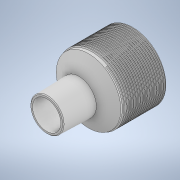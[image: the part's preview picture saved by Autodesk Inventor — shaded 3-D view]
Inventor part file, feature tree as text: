
AUTODESK INVENTOR PART (.ipt)
format: ipt  version: 2020 (Build 240168000, 168)  size: 853,504 bytes
history: native  units: mm
features: sketch x14, extrude x9, chamfer x6, revolve x3, helix x2, plane x2, split x1, projected_geometry x1
ambient origin geometry x8: Origin, YZ Plane, XZ Plane, XY Plane, X Axis, Y Axis, Z Axis, Center Point
bodies: Solid1 (feature_tree)
feature tree (38):
  extrude  "Extrusion1"  Depth=2.0mm
  chamfer  "Chamfer1"  Distance=2.0mm
  revolve  "Revolution1"  [1 undecoded]
  extrude  "Extrusion2"  Depth=18.75mm
  sketch  "Sketch6"  dims[d17=1.6mm]
  helix  "Coil2"  [1 undecoded]
  chamfer  "Chamfer4"  Distance=10.0mm
  chamfer  "Chamfer5"  Distance=0.65mm Angle=45.0deg
  extrude  "Extrusion4"  Depth=42.0mm
  extrude  "Extrusion6"  Depth=10.0mm
  extrude  "Extrusion7"  Depth=10.0mm
  helix  "Coil3"  [1 undecoded]
  extrude  "Extrusion8"  Depth=10.0mm TaperAngle=0.0deg
  revolve  "Revolution2"  [1 undecoded]
  extrude  "Extrusion9"  Depth=10.0mm TaperAngle=0.0deg
  plane  "Work Plane3"
  split  "Split2"
  revolve  "Revolution3"  [1 undecoded]
  plane  "Work Plane4"
  extrude  "Extrusion10"  Depth=10.0mm
  chamfer  "Chamfer9"  Distance=1.5mm
  chamfer  "Chamfer10"  Distance=45.0mm
  chamfer  "Chamfer13"  Distance=20.0mm
  extrude  "Extrusion11"  TaperAngle=135.0deg  [1 undecoded]
  sketch  "Sketch1"  dims[d0=18.0mm d1=2.0mm d2=2.0mm d3=0.0mm]
  sketch  "Sketch4"  dims[d4=2.0mm d5=2.0mm d6=45.0deg d10=12.25mm]
  sketch  "Sketch5"  dims[d11=8.0mm d12=18.75mm d14=1.5mm]
  projected_geometry  "Projected Loop1"
  sketch  "Sketch8"  dims[d18=90.0deg d19=10.0mm d20=0.0mm]
  sketch  "Sketch9"  dims[d21=1.0mm]
  sketch  "Sketch10"  dims[d22=1.0mm]
  sketch  "Sketch11"  dims[d23=1.5mm]
  sketch  "Sketch12"  dims[d24=0.8mm]
  sketch  "Sketch13"  dims[d42=0.1mm]
  sketch  "Sketch14"  dims[d43=1.5mm]
  sketch  "Sketch15"  dims[d44=6.0mm d45=10.0mm d46=0.0mm d47=90.0deg d48=90.0deg d49=0.0mm d50=0.0mm d51=0.65mm d52=4.0mm d53=45.0deg]
  sketch  "Sketch19"  dims[d54=0.65mm d55=4.0mm d56=45.0deg d57=42.0mm]
  sketch  "Sketch20"  dims[d58=28.0mm d59=0.0mm d60=2.65mm d61=1.2mm d62=1.2mm d65=12.0mm d66=0.0mm d67=30.0mm d68=3.0mm d69=0.0mm d74=1.0mm d75=0.65mm d76=1.5mm d77=28.0mm d78=10.0mm d79=0.0mm d80=90.0deg d81=90.0deg d82=0.0mm d83=0.0mm d84=45.0mm d85=20.0mm d86=0.0mm d87=135.0deg d88=90.0deg d90=0.7mm d91=0.0mm d92=0.0mm d95=21.0mm d96=10.81mm d97=1.6mm d98=1.6mm d99=6.981317mm d100=90.0deg d101=0.75mm d102=1.4mm d117=45.0deg d120=10.0mm d121=12.0mm d122=12.0mm d123=0.0mm d124=0.0mm d131=0.5mm d132=2.0mm d133=45.0deg d136=3.0mm d137=2.0mm d138=45.0deg d146=2.15mm d147=2.0mm d148=45.0deg d149=0.75mm d150=0.75mm d151=8.0mm d152=10.0mm d153=0.0mm d157=15.0mm d158=11.185mm d70=0.5mm d71=0.872665mm d72=0.5mm d73=0.872665mm d89=0.5mm]
note: 6 required parameter values undecoded (feature->parameter linkage not recoverable at this tier; creation-order binding heuristic only, values carry confidence <= 0.55)